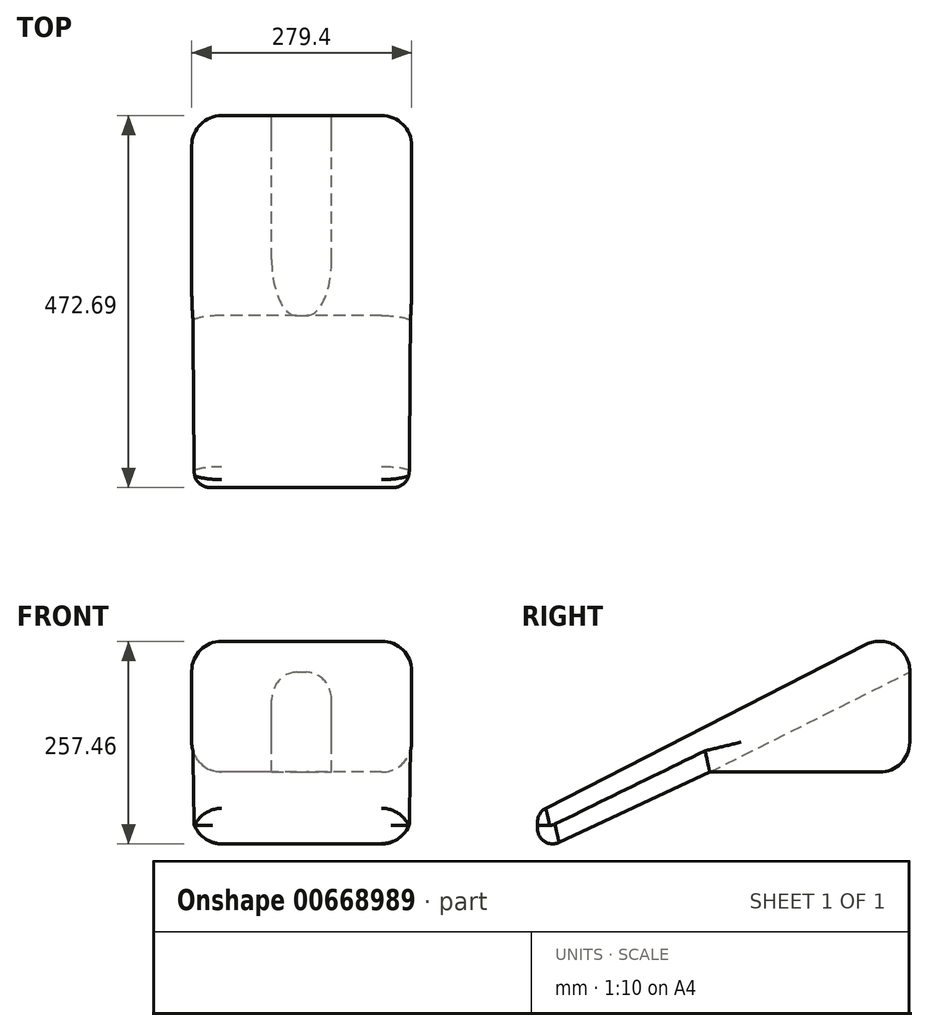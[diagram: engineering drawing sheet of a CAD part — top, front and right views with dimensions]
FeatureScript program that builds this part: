
annotation { "Feature Type Name" : "Feature", "Feature Type Description" : "" }
export const myFeature = defineFeature(function(context is Context, id is Id, definition is map)
    precondition{}
    {
        {
            var Q0;
            Q0=qCreatedBy(makeId("Right.planeOp"),FACE);
            var sketch = newSketch(context, id + "F0", { "sketchPlane" : qUnion([Q0])});
            skLineSegment(sketch, "E0", {"start": v(0, 0) * mm, "end": v(254, 0) * mm});
            skLineSegment(sketch, "E1", {"start": v(254, 0) * mm, "end": v(254, 190.5) * mm});
            skLineSegment(sketch, "E2", {"start": v(254, 190.5) * mm, "end": v(-218.7, -51.18) * mm});
            skLineSegment(sketch, "E3", {"start": v(-218.7, -51.18) * mm, "end": v(-218.7, -101.98) * mm});
            skLineSegment(sketch, "E4", {"start": v(-218.7, -101.98) * mm, "end": v(0, 0) * mm});
            skSolve(sketch);
        }
        {
            var Q0;
            Q0=makeQuery(id+"F0.imprint","IMPRINT",FACE,{"disambiguationData":[TD([[makeQuery(id+"F0.imprint","IMPRINT",EDGE,{"derivedFrom":sQuery(id+"F0.wireOp",EDGE,"E0")}),1.0]])]});
            extrude(context, id + "F1", {"entities" : qUnion([Q0]), "endBound" : BoundingType.SYMMETRIC, "depth" : 279.4 * mm, "offsetDistance" : 25.4 * mm});
        }
        {
            var Q0;
            Q0=qCreatedBy(makeId("Right.planeOp"),FACE);
            var sketch = newSketch(context, id + "F2", { "sketchPlane" : qUnion([Q0])});
            skLineSegment(sketch, "E5.0", {"start": v(254, 0) * mm, "end": v(254, 190.5) * mm});
            skLineSegment(sketch, "E6.0", {"start": v(-218.7, -101.98) * mm, "end": v(0, 0) * mm});
            skLineSegment(sketch, "E7", {"start": v(0, 0) * mm, "end": v(254, 127) * mm});
            skLineSegment(sketch, "E8", {"start": v(254, 127) * mm, "end": v(254, 0) * mm});
            skLineSegment(sketch, "E9", {"start": v(0, 0) * mm, "end": v(254, 0) * mm});
            skSolve(sketch);
        }
        {
            var Q0;
            Q0 = qSketchRegion(id + "F2", true);
            extrude(context, id + "F3", {"entities" : qUnion([Q0]), "operationType" : NewBodyOperationType.REMOVE, "endBound" : BoundingType.SYMMETRIC, "oppositeDirection" : true, "depth" : 76.2 * mm, "offsetDistance" : 25.4 * mm});
        }
        {
            var Q0;
            Q0=makeQuery(id+"F1.opExtrude","SWEPT_EDGE",EDGE,{"disambiguationData":[OSD([sQuery(id+"F0.wireOp",EDGE,"E1"),sQuery(id+"F0.wireOp",EDGE,"E2")])]});
            var Q1;
            {var subQ0=sQuery(id+"F0.wireOp",EDGE,"E0");var subQ1=sQuery(id+"F0.wireOp",EDGE,"E1");Q1=makeQuery(id+"F3.boolean.opBoolean","SPLIT",EDGE,{"disambiguationData":[TD([makeQuery(id+"F3.opExtrude","CAP_FACE",FACE,{"disambiguationData":[OSD([sQuery(id+"F2.wireOp",EDGE,"E7"),sQuery(id+"F2.wireOp",EDGE,"E8"),sQuery(id+"F2.wireOp",EDGE,"E9")])],"isStart":true})])],"derivedFrom":makeQuery(id+"F1.opExtrude","SWEPT_EDGE",EDGE,{"disambiguationData":[OSD([subQ0,subQ1])]})});}
            var Q2;
            {var subQ0=sQuery(id+"F0.wireOp",EDGE,"E0");var subQ1=sQuery(id+"F0.wireOp",EDGE,"E1");Q2=makeQuery(id+"F3.boolean.opBoolean","SPLIT",EDGE,{"disambiguationData":[TD([makeQuery(id+"F3.opExtrude","CAP_FACE",FACE,{"disambiguationData":[OSD([sQuery(id+"F2.wireOp",EDGE,"E7"),sQuery(id+"F2.wireOp",EDGE,"E8"),sQuery(id+"F2.wireOp",EDGE,"E9")])],"isStart":false})])],"derivedFrom":makeQuery(id+"F1.opExtrude","SWEPT_EDGE",EDGE,{"disambiguationData":[OSD([subQ0,subQ1])]})});}
            fillet(context, id + "F4", {"entities" : qUnion([Q0, Q1, Q2]), "radius" : 38.1 * mm, "tangentPropagation" : true, "allowEdgeOverflow" : false});
        }
        {
            var Q0;
            Q0=makeQuery(id+"F1.opExtrude","CAP_EDGE",EDGE,{"disambiguationData":[OSD([sQuery(id+"F0.wireOp",EDGE,"E1")])],"isStart":false});
            var Q1;
            Q1=makeQuery(id+"F1.opExtrude","CAP_EDGE",EDGE,{"disambiguationData":[OSD([sQuery(id+"F0.wireOp",EDGE,"E4")])],"isStart":false});
            var Q2;
            Q2=makeQuery(id+"F1.opExtrude","CAP_EDGE",EDGE,{"disambiguationData":[OSD([sQuery(id+"F0.wireOp",EDGE,"E2")])],"isStart":true});
            var Q3;
            Q3=makeQuery(id+"F1.opExtrude","CAP_EDGE",EDGE,{"disambiguationData":[OSD([sQuery(id+"F0.wireOp",EDGE,"E4")])],"isStart":true});
            fillet(context, id + "F5", {"entities" : qUnion([Q0, Q1, Q2, Q3]), "radius" : 38.1 * mm, "tangentPropagation" : true, "allowEdgeOverflow" : false});
        }
        {
            var Q0;
            Q0=makeQuery(id+"F1.opExtrude","SWEPT_EDGE",EDGE,{"disambiguationData":[OSD([sQuery(id+"F0.wireOp",EDGE,"E2"),sQuery(id+"F0.wireOp",EDGE,"E3")])]});
            var Q1;
            Q1=makeQuery(id+"F1.opExtrude","SWEPT_EDGE",EDGE,{"disambiguationData":[OSD([sQuery(id+"F0.wireOp",EDGE,"E3"),sQuery(id+"F0.wireOp",EDGE,"E4")])]});
            var Q2;
            Q2=makeQuery(id+"F5.opFillet","BLEND_EDGE",EDGE,{"blendedFrom":[makeQuery(id+"F1.opExtrude","CAP_EDGE",EDGE,{"disambiguationData":[OSD([sQuery(id+"F0.wireOp",EDGE,"E2")])],"isStart":false}),makeQuery(id+"F1.opExtrude","SWEPT_FACE",FACE,{"disambiguationData":[OSD([sQuery(id+"F0.wireOp",EDGE,"E3")])]})],"blendedInto":[makeQuery(id+"F1.opExtrude","SWEPT_FACE",FACE,{"disambiguationData":[OSD([sQuery(id+"F0.wireOp",EDGE,"E3")])]})]});
            var Q3;
            Q3=makeQuery(id+"F5.opFillet","BLEND_EDGE",EDGE,{"blendedFrom":[makeQuery(id+"F1.opExtrude","CAP_EDGE",EDGE,{"disambiguationData":[OSD([sQuery(id+"F0.wireOp",EDGE,"E4")])],"isStart":true}),makeQuery(id+"F1.opExtrude","SWEPT_FACE",FACE,{"disambiguationData":[OSD([sQuery(id+"F0.wireOp",EDGE,"E3")])]})],"blendedInto":[makeQuery(id+"F1.opExtrude","SWEPT_FACE",FACE,{"disambiguationData":[OSD([sQuery(id+"F0.wireOp",EDGE,"E3")])]})]});
            var Q4;
            Q4=makeQuery(id+"F5.opFillet","BLEND_EDGE",EDGE,{"blendedFrom":[makeQuery(id+"F1.opExtrude","CAP_EDGE",EDGE,{"disambiguationData":[OSD([sQuery(id+"F0.wireOp",EDGE,"E2")])],"isStart":true}),makeQuery(id+"F1.opExtrude","SWEPT_FACE",FACE,{"disambiguationData":[OSD([sQuery(id+"F0.wireOp",EDGE,"E3")])]})],"blendedInto":[makeQuery(id+"F1.opExtrude","SWEPT_FACE",FACE,{"disambiguationData":[OSD([sQuery(id+"F0.wireOp",EDGE,"E3")])]})]});
            fillet(context, id + "F6", {"entities" : qUnion([Q0, Q1, Q2, Q3, Q4]), "radius" : 19.05 * mm, "tangentPropagation" : true, "allowEdgeOverflow" : false});
        }
        {
            var Q0;
            Q0=makeQuery(id+"F3.boolean.opBoolean","COPY",EDGE,{"derivedFrom":makeQuery(id+"F3.opExtrude","CAP_EDGE",EDGE,{"disambiguationData":[OSD([sQuery(id+"F2.wireOp",EDGE,"E7")])],"isStart":true})});
            var Q1;
            Q1=makeQuery(id+"F3.boolean.opBoolean","COPY",EDGE,{"derivedFrom":makeQuery(id+"F3.opExtrude","CAP_EDGE",EDGE,{"disambiguationData":[OSD([sQuery(id+"F2.wireOp",EDGE,"E7")])],"isStart":false})});
            fillet(context, id + "F7", {"entities" : qUnion([Q0, Q1]), "radius" : 31.75 * mm, "tangentPropagation" : true, "allowEdgeOverflow" : false});
        }
    });
